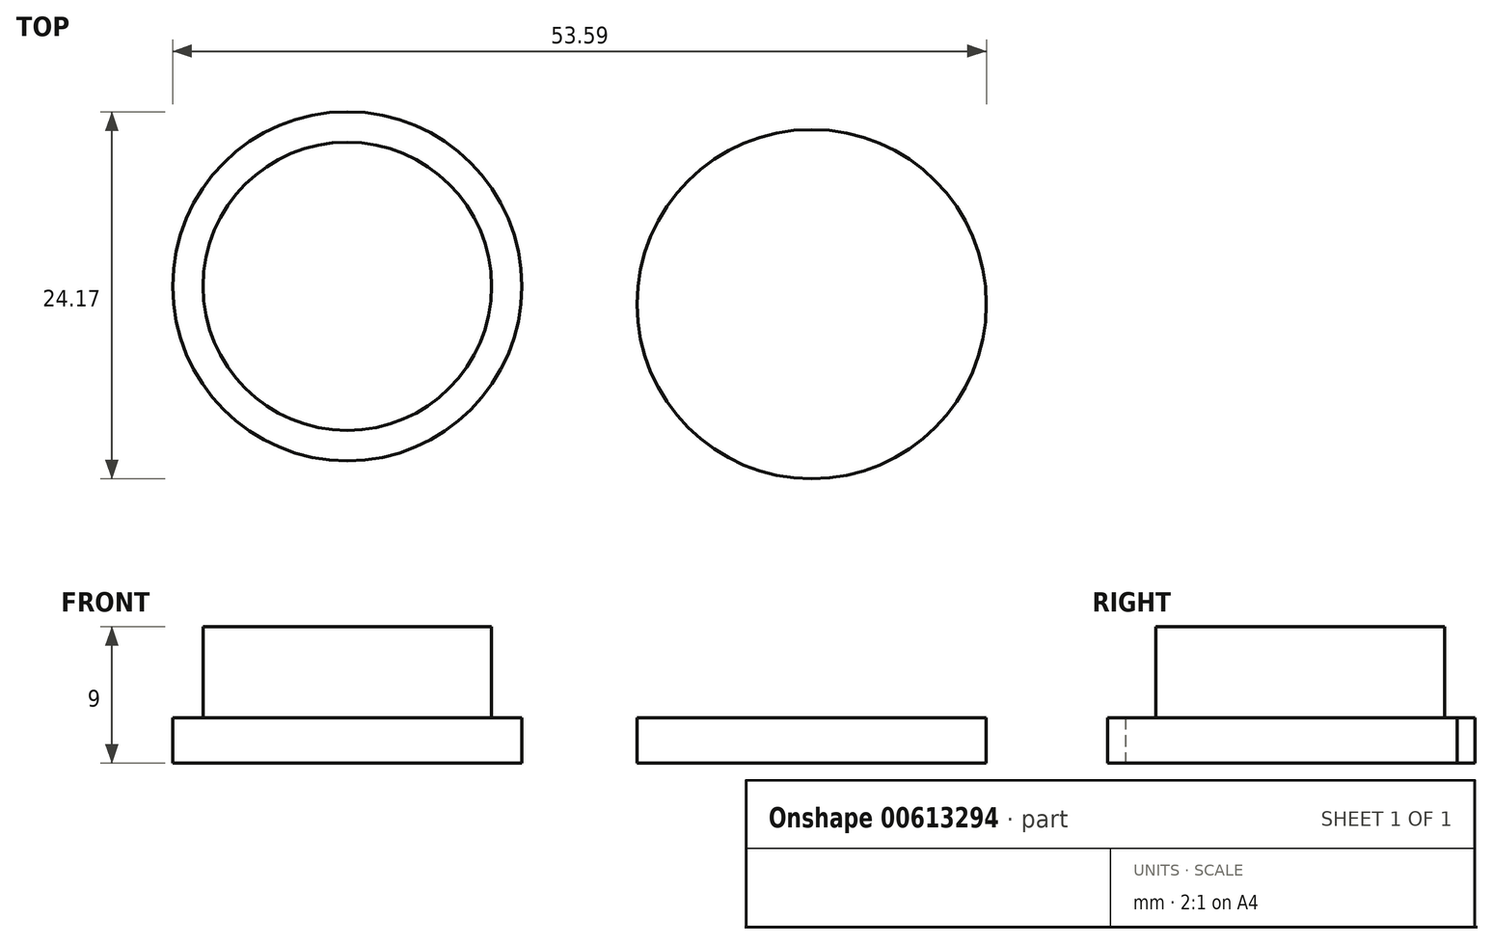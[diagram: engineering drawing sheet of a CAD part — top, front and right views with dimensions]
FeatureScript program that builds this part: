
annotation { "Feature Type Name" : "Feature", "Feature Type Description" : "" }
export const myFeature = defineFeature(function(context is Context, id is Id, definition is map)
    precondition{}
    {
        {
            var Q0;
            Q0=qCreatedBy(makeId("Top.planeOp"),FACE);
            var sketch = newSketch(context, id + "F0", { "sketchPlane" : qUnion([Q0])});
            skCircle(sketch, "E0", {"center": v(-47.32, -50.02) * mm, "radius": 11.5 * mm});
            skCircle(sketch, "E1", {"center": v(-47.32, -50.02) * mm, "radius": 9.5 * mm});
            skSolve(sketch);
        }
        {
            var Q0;
            Q0=makeQuery(id+"F0.imprint","IMPRINT",FACE,{"disambiguationData":[TD([[makeQuery(id+"F0.imprint","IMPRINT",EDGE,{"derivedFrom":sQuery(id+"F0.wireOp",EDGE,"E1")}),1.0]])]});
            extrude(context, id + "F1", {"entities" : qUnion([Q0]), "depth" : 9 * mm, "offsetDistance" : 25 * mm});
        }
        {
            var Q0;
            Q0=makeQuery(id+"F0.imprint","IMPRINT",FACE,{"disambiguationData":[TD([[makeQuery(id+"F0.imprint","IMPRINT",EDGE,{"derivedFrom":sQuery(id+"F0.wireOp",EDGE,"E0")}),1.0]])]});
            extrude(context, id + "F2", {"entities" : qUnion([Q0]), "operationType" : NewBodyOperationType.ADD, "depth" : 3 * mm, "offsetDistance" : 25 * mm});
        }
        {
            var Q0;
            Q0=qCreatedBy(makeId("Top.planeOp"),FACE);
            var sketch = newSketch(context, id + "F3", { "sketchPlane" : qUnion([Q0])});
            skCircle(sketch, "E2", {"center": v(-16.73, -51.2) * mm, "radius": 11.5 * mm});
            skSolve(sketch);
        }
        {
            var Q0;
            Q0=makeQuery(id+"F3.imprint","IMPRINT",FACE,{"disambiguationData":[TD([[makeQuery(id+"F3.imprint","IMPRINT",EDGE,{"derivedFrom":sQuery(id+"F3.wireOp",EDGE,"E2")}),1.0]])]});
            extrude(context, id + "F4", {"entities" : qUnion([Q0]), "depth" : 3 * mm, "offsetDistance" : 25 * mm});
        }
        {
            var Q0;
            Q0=makeQuery(id+"F1.opExtrude","SWEPT_BODY",BODY,{"disambiguationData":[OSD([sQuery(id+"F0.wireOp",EDGE,"E1")])]});
            transform(context, id + "F5", {"entities" : qUnion([Q0]), "transformType" : TransformType.TRANSLATION_3D, "dx" : 0 * mm, "dy" : 0 * mm, "dz" : 0 * mm, "makeCopy" : true});
        }
    });
